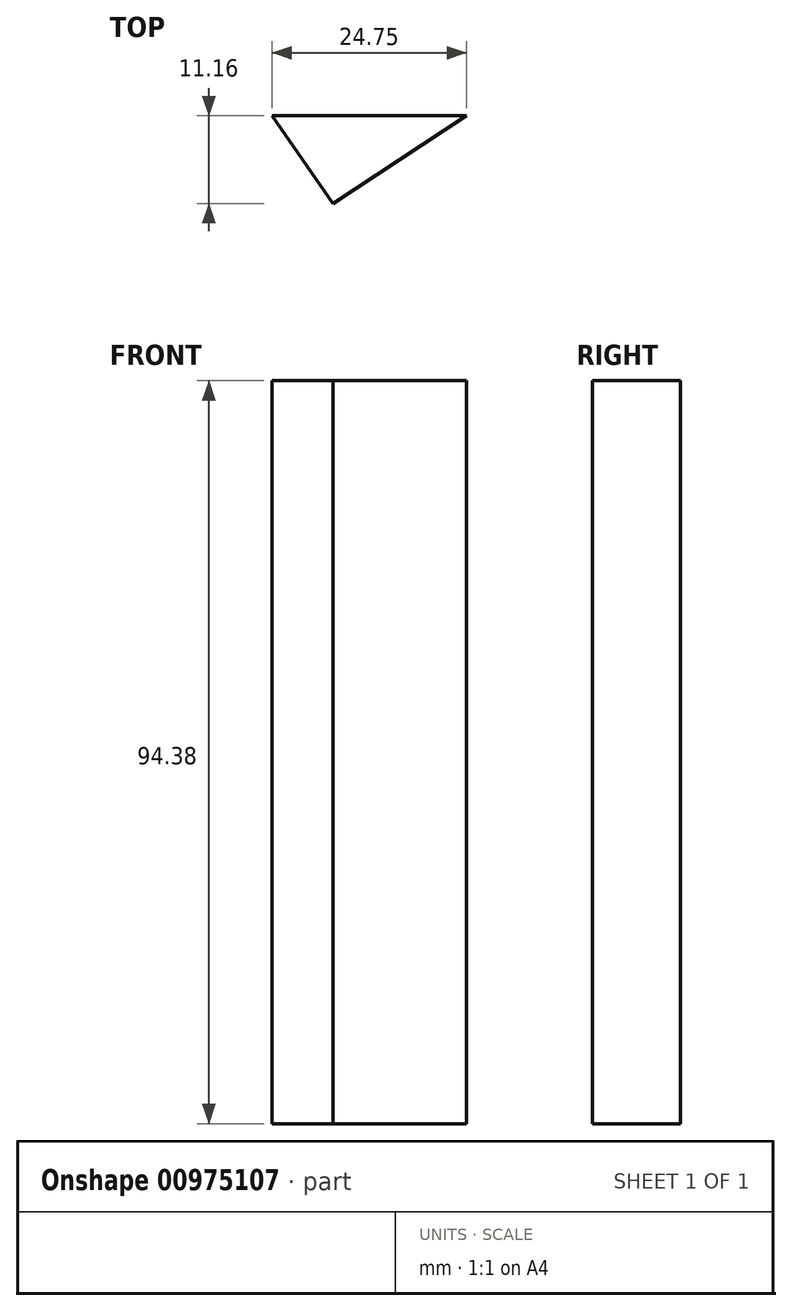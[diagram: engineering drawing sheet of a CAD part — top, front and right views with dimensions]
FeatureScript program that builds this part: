
annotation { "Feature Type Name" : "Feature", "Feature Type Description" : "" }
export const myFeature = defineFeature(function(context is Context, id is Id, definition is map)
    precondition{}
    {
        {
            var Q0;
            Q0=qCreatedBy(makeId("Top.planeOp"),FACE);
            var sketch = newSketch(context, id + "F0", { "sketchPlane" : qUnion([Q0])});
            skLineSegment(sketch, "E0", {"start": v(-49.2, 37.34) * mm, "end": v(-49.2, -7.34) * mm});
            skLineSegment(sketch, "E1", {"start": v(-49.2, -7.34) * mm, "end": v(-49.2, 15) * mm});
            skLineSegment(sketch, "E2", {"start": v(-49.2, 24) * mm, "end": v(-40.04, 35.85) * mm});
            skLineSegment(sketch, "E3", {"start": v(-40.04, 35.85) * mm, "end": v(-34.5, 13.8) * mm});
            skLineSegment(sketch, "E4", {"start": v(-34.5, 13.8) * mm, "end": v(-35.55, -8.1) * mm});
            skLineSegment(sketch, "E5", {"start": v(-35.55, -8.1) * mm, "end": v(-51.14, -25.5) * mm});
            skLineSegment(sketch, "E6", {"start": v(-51.14, -25.5) * mm, "end": v(-62.4, -3.9) * mm});
            skLineSegment(sketch, "E7", {"start": v(-62.4, -3.9) * mm, "end": v(-61.34, 20.25) * mm});
            skLineSegment(sketch, "E8", {"start": v(-61.34, 20.25) * mm, "end": v(-60.3, 37.34) * mm});
            skLineSegment(sketch, "E9", {"start": v(-60.3, 37.34) * mm, "end": v(-46.34, 46.64) * mm});
            skLineSegment(sketch, "E10", {"start": v(-46.34, 46.64) * mm, "end": v(-34.95, 49.64) * mm});
            skLineSegment(sketch, "E11", {"start": v(-34.95, 49.64) * mm, "end": v(-10.35, 65.84) * mm});
            skLineSegment(sketch, "E12", {"start": v(-10.35, 65.84) * mm, "end": v(-35.1, 65.84) * mm});
            skLineSegment(sketch, "E13", {"start": v(-35.1, 65.84) * mm, "end": v(-9.37, 28.99) * mm});
            skLineSegment(sketch, "E14", {"start": v(-9.37, 28.99) * mm, "end": v(108.64, 66.28) * mm});
            skLineSegment(sketch, "E15", {"start": v(108.64, 66.28) * mm, "end": v(-57.29, 130.75) * mm, "construction": true});
            skLineSegment(sketch, "E16", {"start": v(-9.37, 28.99) * mm, "end": v(-35.02, 2.85) * mm});
            skLineSegment(sketch, "E17", {"start": v(-35.02, 2.85) * mm, "end": v(-22.23, 47.42) * mm});
            skLineSegment(sketch, "E18.bottom", {"start": v(-14.1, -89.3) * mm, "end": v(53.41, -89.3) * mm, "construction": true});
            skLineSegment(sketch, "E18.top", {"start": v(-14.1, -141.94) * mm, "end": v(53.41, -141.94) * mm, "construction": true});
            skLineSegment(sketch, "E18.left", {"start": v(-14.1, -89.3) * mm, "end": v(-14.1, -141.94) * mm, "construction": true});
            skLineSegment(sketch, "E18.right", {"start": v(53.41, -89.3) * mm, "end": v(53.41, -141.94) * mm, "construction": true});
            skSolve(sketch);
        }
        {
            var Q0;
            {var subQ0=sQuery(id+"F0.wireOp",EDGE,"E12");Q0=makeQuery(id+"F0.imprint","IMPRINT",FACE,{"disambiguationData":[TD([[makeQuery(id+"F0.imprint","IMPRINT",EDGE,{"derivedFrom":subQ0}),1.0]])]});}
            extrude(context, id + "F1", {"entities" : qUnion([Q0]), "oppositeDirection" : true, "depth" : 94.38 * mm, "offsetDistance" : 25.4 * mm});
        }
    });
